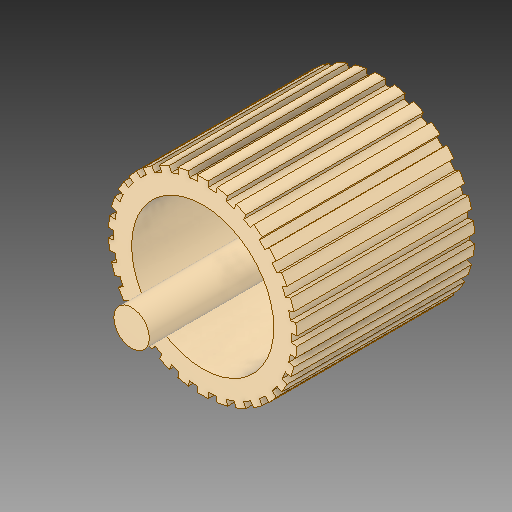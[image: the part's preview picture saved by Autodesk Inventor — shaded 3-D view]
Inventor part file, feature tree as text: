
AUTODESK INVENTOR PART (.ipt)
format: ipt  version: 2018.1 (Build 221171000, 171)  size: 357,376 bytes
history: native  units: mm
features: extrude x3, sketch x3, other x1
ambient origin geometry x8: Origin, YZ Plane, XZ Plane, XY Plane, X Axis, Y Axis, Z Axis, Center Point
bodies: Body1 (feature_tree)
feature tree (7):
  other  "ソリッド1"
  extrude  "押し出し1"  Depth=50.0mm
  extrude  "押し出し2"  Depth=3.0mm
  extrude  "押し出し3"  Depth=3.0mm
  sketch  "スケッチ1"
  sketch  "スケッチ2"
  sketch  "スケッチ3"
